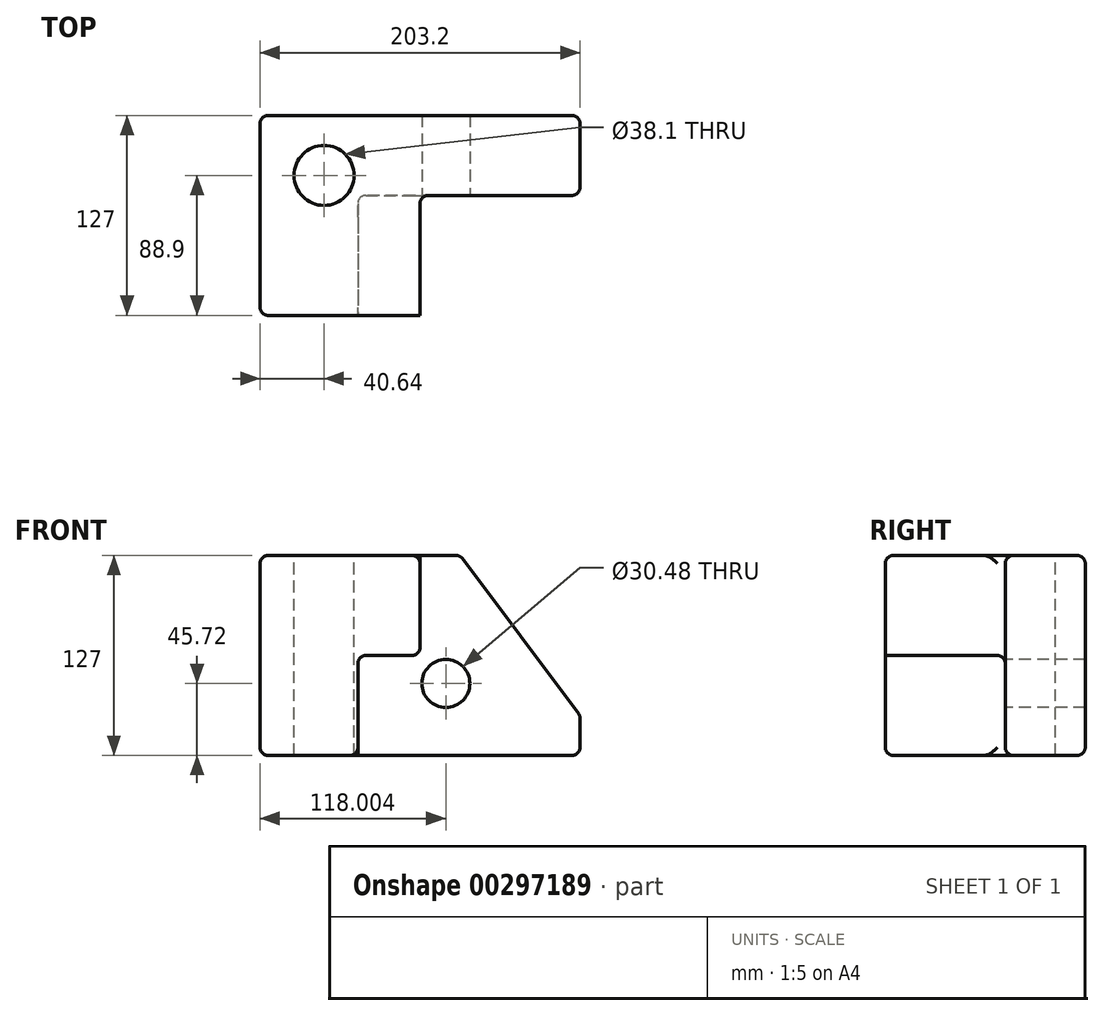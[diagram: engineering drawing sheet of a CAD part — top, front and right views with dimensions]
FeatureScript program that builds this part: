
annotation { "Feature Type Name" : "Feature", "Feature Type Description" : "" }
export const myFeature = defineFeature(function(context is Context, id is Id, definition is map)
    precondition{}
    {
        {
            var Q0;
            Q0=qCreatedBy(makeId("Front.planeOp"),FACE);
            var sketch = newSketch(context, id + "F0", { "sketchPlane" : qUnion([Q0])});
            skLineSegment(sketch, "E0.bottom", {"start": v(101.6, 63.5) * mm, "end": v(-101.6, 63.5) * mm});
            skLineSegment(sketch, "E0.top", {"start": v(101.6, -63.5) * mm, "end": v(-101.6, -63.5) * mm});
            skLineSegment(sketch, "E0.left", {"start": v(101.6, 63.5) * mm, "end": v(101.6, -63.5) * mm});
            skLineSegment(sketch, "E0.right", {"start": v(-101.6, 63.5) * mm, "end": v(-101.6, -63.5) * mm});
            skPoint(sketch, "E0.middle", {"position": v(0, 0) * mm});
            skSolve(sketch);
        }
        {
            var Q0;
            Q0 = qSketchRegion(id + "F0", true);
            extrude(context, id + "F1", {"entities" : qUnion([Q0]), "oppositeDirection" : true, "depth" : 127 * mm});
        }
        {
            var Q0;
            Q0=makeQuery(id+"F1.opExtrude","CAP_FACE",FACE,{"disambiguationData":[OSD([sQuery(id+"F0.wireOp",EDGE,"E0.bottom"),sQuery(id+"F0.wireOp",EDGE,"E0.top"),sQuery(id+"F0.wireOp",EDGE,"E0.left"),sQuery(id+"F0.wireOp",EDGE,"E0.right")])],"isStart":true});
            var sketch = newSketch(context, id + "F2", { "sketchPlane" : qUnion([Q0])});
            skLineSegment(sketch, "E1", {"start": v(-39.48, -63.5) * mm, "end": v(-39.48, 0) * mm});
            skLineSegment(sketch, "E2", {"start": v(-39.48, 0) * mm, "end": v(0, 0) * mm});
            skLineSegment(sketch, "E3", {"start": v(0, 0) * mm, "end": v(0, 63.5) * mm});
            skSolve(sketch);
        }
        {
            var Q0;
            {var subQ2=sQuery(id+"F2.wireOp",EDGE,"E1");Q0=makeQuery(id+"F2.imprint","IMPRINT",FACE,{"disambiguationData":[TD([[makeQuery(id+"F2.imprint","IMPRINT",EDGE,{"derivedFrom":subQ2}),-1.0]])]});}
            extrude(context, id + "F3", {"entities" : qUnion([Q0]), "operationType" : NewBodyOperationType.REMOVE, "oppositeDirection" : true, "depth" : 76.2 * mm});
        }
        {
            var Q0;
            Q0=makeQuery(id+"F1.opExtrude","SWEPT_EDGE",EDGE,{"disambiguationData":[OSD([sQuery(id+"F0.wireOp",EDGE,"E0.bottom"),sQuery(id+"F0.wireOp",EDGE,"E0.left")])]});
            chamfer(context, id + "F4", {"entities" : qUnion([Q0]), "chamferType" : ChamferType.TWO_OFFSETS, "width1" : 76.2 * mm, "oppositeDirection" : true, "width2" : 101.6 * mm, "tangentPropagation" : true});
        }
        {
            var Q0;
            Q0=makeQuery(id+"F1.opExtrude","SWEPT_EDGE",EDGE,{"disambiguationData":[OSD([sQuery(id+"F0.wireOp",EDGE,"E0.top"),sQuery(id+"F0.wireOp",EDGE,"E0.left")])]});
            var Q1;
            {var subQ0=sQuery(id+"F0.wireOp",EDGE,"E0.left");Q1=makeQuery(id+"F4.opChamfer","BLEND_EDGE",EDGE,{"blendedFrom":[makeQuery(id+"F1.opExtrude","SWEPT_EDGE",EDGE,{"disambiguationData":[OSD([sQuery(id+"F0.wireOp",EDGE,"E0.bottom"),subQ0])]}),makeQuery(id+"F1.opExtrude","SWEPT_FACE",FACE,{"disambiguationData":[OSD([subQ0])]})],"blendedInto":[makeQuery(id+"F1.opExtrude","SWEPT_FACE",FACE,{"disambiguationData":[OSD([subQ0])]})]});}
            var Q2;
            {var subQ0=sQuery(id+"F0.wireOp",EDGE,"E0.bottom");Q2=makeQuery(id+"F4.opChamfer","BLEND_EDGE",EDGE,{"blendedFrom":[makeQuery(id+"F1.opExtrude","SWEPT_EDGE",EDGE,{"disambiguationData":[OSD([subQ0,sQuery(id+"F0.wireOp",EDGE,"E0.left")])]}),makeQuery(id+"F1.opExtrude","SWEPT_FACE",FACE,{"disambiguationData":[OSD([subQ0])]})],"blendedInto":[makeQuery(id+"F1.opExtrude","SWEPT_FACE",FACE,{"disambiguationData":[OSD([subQ0])]})]});}
            var Q3;
            {var subQ0=sQuery(id+"F0.wireOp",EDGE,"E0.left");var subQ1=sQuery(id+"F0.wireOp",EDGE,"E0.bottom");Q3=makeQuery(id+"F4.opChamfer","BLEND_EDGE",EDGE,{"blendedFrom":[makeQuery(id+"F1.opExtrude","SWEPT_EDGE",EDGE,{"disambiguationData":[OSD([subQ1,subQ0])]}),makeQuery(id+"F3.boolean.opBoolean","COPY",FACE,{"derivedFrom":makeQuery(id+"F3.opExtrude","CAP_FACE",FACE,{"disambiguationData":[OSD([subQ1,sQuery(id+"F0.wireOp",EDGE,"E0.top"),subQ0,sQuery(id+"F2.wireOp",EDGE,"E1"),sQuery(id+"F2.wireOp",EDGE,"E2"),sQuery(id+"F2.wireOp",EDGE,"E3")])],"isStart":false})})],"blendedInto":[makeQuery(id+"F3.boolean.opBoolean","COPY",FACE,{"derivedFrom":makeQuery(id+"F3.opExtrude","CAP_FACE",FACE,{"disambiguationData":[OSD([subQ1,sQuery(id+"F0.wireOp",EDGE,"E0.top"),subQ0,sQuery(id+"F2.wireOp",EDGE,"E1"),sQuery(id+"F2.wireOp",EDGE,"E2"),sQuery(id+"F2.wireOp",EDGE,"E3")])],"isStart":false})})]});}
            var Q4;
            {var subQ0=sQuery(id+"F0.wireOp",EDGE,"E0.left");var subQ1=sQuery(id+"F0.wireOp",EDGE,"E0.bottom");Q4=makeQuery(id+"F4.opChamfer","BLEND_EDGE",EDGE,{"blendedFrom":[makeQuery(id+"F1.opExtrude","SWEPT_EDGE",EDGE,{"disambiguationData":[OSD([subQ1,subQ0])]}),makeQuery(id+"F1.opExtrude","CAP_FACE",FACE,{"disambiguationData":[OSD([subQ1,sQuery(id+"F0.wireOp",EDGE,"E0.top"),subQ0,sQuery(id+"F0.wireOp",EDGE,"E0.right")])],"isStart":false})],"blendedInto":[makeQuery(id+"F1.opExtrude","CAP_FACE",FACE,{"disambiguationData":[OSD([subQ1,sQuery(id+"F0.wireOp",EDGE,"E0.top"),subQ0,sQuery(id+"F0.wireOp",EDGE,"E0.right")])],"isStart":false})]});}
            var Q5;
            Q5=makeQuery(id+"F3.boolean.opBoolean","COPY",EDGE,{"derivedFrom":makeQuery(id+"F3.opExtrude","CAP_EDGE",EDGE,{"disambiguationData":[OSD([sQuery(id+"F0.wireOp",EDGE,"E0.bottom")])],"isStart":false})});
            var Q6;
            Q6=makeQuery(id+"F3.boolean.opBoolean","COPY",EDGE,{"derivedFrom":makeQuery(id+"F3.opExtrude","SWEPT_EDGE",EDGE,{"disambiguationData":[OSD([sQuery(id+"F0.wireOp",EDGE,"E0.bottom"),sQuery(id+"F2.wireOp",EDGE,"E3")])]})});
            var Q7;
            Q7=makeQuery(id+"F3.boolean.opBoolean","COPY",EDGE,{"derivedFrom":makeQuery(id+"F3.opExtrude","SWEPT_EDGE",EDGE,{"disambiguationData":[OSD([sQuery(id+"F2.wireOp",EDGE,"E2"),sQuery(id+"F2.wireOp",EDGE,"E3")])]})});
            var Q8;
            Q8=makeQuery(id+"F3.boolean.opBoolean","COPY",FACE,{"derivedFrom":makeQuery(id+"F3.opExtrude","CAP_FACE",FACE,{"disambiguationData":[OSD([sQuery(id+"F0.wireOp",EDGE,"E0.bottom"),sQuery(id+"F0.wireOp",EDGE,"E0.top"),sQuery(id+"F0.wireOp",EDGE,"E0.left"),sQuery(id+"F2.wireOp",EDGE,"E1"),sQuery(id+"F2.wireOp",EDGE,"E2"),sQuery(id+"F2.wireOp",EDGE,"E3")])],"isStart":false})});
            var Q9;
            Q9=makeQuery(id+"F3.boolean.opBoolean","COPY",EDGE,{"derivedFrom":makeQuery(id+"F3.opExtrude","CAP_EDGE",EDGE,{"disambiguationData":[OSD([sQuery(id+"F0.wireOp",EDGE,"E0.top")])],"isStart":false})});
            var Q10;
            Q10=makeQuery(id+"F3.boolean.opBoolean","COPY",EDGE,{"derivedFrom":makeQuery(id+"F3.opExtrude","CAP_EDGE",EDGE,{"disambiguationData":[OSD([sQuery(id+"F2.wireOp",EDGE,"E1")])],"isStart":true})});
            var Q11;
            Q11=makeQuery(id+"F3.boolean.opBoolean","COPY",EDGE,{"derivedFrom":makeQuery(id+"F3.opExtrude","CAP_EDGE",EDGE,{"disambiguationData":[OSD([sQuery(id+"F2.wireOp",EDGE,"E2")])],"isStart":true})});
            var Q12;
            Q12=makeQuery(id+"F1.opExtrude","CAP_EDGE",EDGE,{"disambiguationData":[OSD([sQuery(id+"F0.wireOp",EDGE,"E0.bottom")])],"isStart":true});
            var Q13;
            Q13=makeQuery(id+"F3.boolean.opBoolean","COPY",EDGE,{"derivedFrom":makeQuery(id+"F3.opExtrude","CAP_EDGE",EDGE,{"disambiguationData":[OSD([sQuery(id+"F2.wireOp",EDGE,"E3")])],"isStart":true})});
            var Q14;
            Q14=makeQuery(id+"F1.opExtrude","SWEPT_EDGE",EDGE,{"disambiguationData":[OSD([sQuery(id+"F0.wireOp",EDGE,"E0.bottom"),sQuery(id+"F0.wireOp",EDGE,"E0.right")])]});
            var Q15;
            Q15=makeQuery(id+"F1.opExtrude","CAP_EDGE",EDGE,{"disambiguationData":[OSD([sQuery(id+"F0.wireOp",EDGE,"E0.bottom")])],"isStart":false});
            var Q16;
            Q16=makeQuery(id+"F1.opExtrude","CAP_EDGE",EDGE,{"disambiguationData":[OSD([sQuery(id+"F0.wireOp",EDGE,"E0.top")])],"isStart":true});
            var Q17;
            Q17=makeQuery(id+"F1.opExtrude","CAP_EDGE",EDGE,{"disambiguationData":[OSD([sQuery(id+"F0.wireOp",EDGE,"E0.right")])],"isStart":true});
            var Q18;
            Q18=makeQuery(id+"F1.opExtrude","SWEPT_EDGE",EDGE,{"disambiguationData":[OSD([sQuery(id+"F0.wireOp",EDGE,"E0.top"),sQuery(id+"F0.wireOp",EDGE,"E0.right")])]});
            var Q19;
            Q19=makeQuery(id+"F3.boolean.opBoolean","COPY",EDGE,{"derivedFrom":makeQuery(id+"F3.opExtrude","SWEPT_EDGE",EDGE,{"disambiguationData":[OSD([sQuery(id+"F2.wireOp",EDGE,"E1"),sQuery(id+"F2.wireOp",EDGE,"E2")])]})});
            var Q20;
            Q20=makeQuery(id+"F3.boolean.opBoolean","COPY",EDGE,{"derivedFrom":makeQuery(id+"F3.opExtrude","CAP_EDGE",EDGE,{"disambiguationData":[OSD([sQuery(id+"F2.wireOp",EDGE,"E3")])],"isStart":false})});
            var Q21;
            Q21=makeQuery(id+"F3.boolean.opBoolean","COPY",EDGE,{"derivedFrom":makeQuery(id+"F3.opExtrude","CAP_EDGE",EDGE,{"disambiguationData":[OSD([sQuery(id+"F0.wireOp",EDGE,"E0.left")])],"isStart":false})});
            var Q22;
            Q22=makeQuery(id+"F1.opExtrude","CAP_EDGE",EDGE,{"disambiguationData":[OSD([sQuery(id+"F0.wireOp",EDGE,"E0.left")])],"isStart":false});
            var Q23;
            Q23=makeQuery(id+"F1.opExtrude","CAP_EDGE",EDGE,{"disambiguationData":[OSD([sQuery(id+"F0.wireOp",EDGE,"E0.top")])],"isStart":false});
            var Q24;
            Q24=makeQuery(id+"F3.boolean.opBoolean","COPY",EDGE,{"derivedFrom":makeQuery(id+"F3.opExtrude","SWEPT_EDGE",EDGE,{"disambiguationData":[OSD([sQuery(id+"F0.wireOp",EDGE,"E0.top"),sQuery(id+"F2.wireOp",EDGE,"E1")])]})});
            var Q25;
            Q25=makeQuery(id+"F3.boolean.opBoolean","COPY",EDGE,{"derivedFrom":makeQuery(id+"F3.opExtrude","CAP_EDGE",EDGE,{"disambiguationData":[OSD([sQuery(id+"F2.wireOp",EDGE,"E2")])],"isStart":false})});
            var Q26;
            Q26=makeQuery(id+"F1.opExtrude","CAP_EDGE",EDGE,{"disambiguationData":[OSD([sQuery(id+"F0.wireOp",EDGE,"E0.right")])],"isStart":false});
            var Q27;
            Q27=makeQuery(id+"F3.boolean.opBoolean","COPY",EDGE,{"derivedFrom":makeQuery(id+"F3.opExtrude","CAP_EDGE",EDGE,{"disambiguationData":[OSD([sQuery(id+"F2.wireOp",EDGE,"E1")])],"isStart":false})});
            fillet(context, id + "F5", {"entities" : qUnion([Q0, Q1, Q2, Q3, Q4, Q5, Q6, Q7, Q8, Q9, Q10, Q11, Q12, Q13, Q14, Q15, Q16, Q17, Q18, Q19, Q20, Q21, Q22, Q23, Q24, Q25, Q26, Q27]), "radius" : 5.08 * mm, "tangentPropagation" : true, "allowEdgeOverflow" : false});
        }
        {
            var Q0;
            Q0=makeQuery(id+"F3.boolean.opBoolean","COPY",FACE,{"derivedFrom":makeQuery(id+"F3.opExtrude","CAP_FACE",FACE,{"disambiguationData":[OSD([sQuery(id+"F0.wireOp",EDGE,"E0.bottom"),sQuery(id+"F0.wireOp",EDGE,"E0.top"),sQuery(id+"F0.wireOp",EDGE,"E0.left"),sQuery(id+"F2.wireOp",EDGE,"E1"),sQuery(id+"F2.wireOp",EDGE,"E2"),sQuery(id+"F2.wireOp",EDGE,"E3")])],"isStart":false})});
            var sketch = newSketch(context, id + "F6", { "sketchPlane" : qUnion([Q0])});
            skCircle(sketch, "E4", {"center": v(16.4, -17.78) * mm, "radius": 15.24 * mm});
            skSolve(sketch);
        }
        {
            var Q0;
            Q0=makeQuery(id+"F6.imprint","IMPRINT",FACE,{"disambiguationData":[TD([[makeQuery(id+"F6.imprint","IMPRINT",EDGE,{"derivedFrom":sQuery(id+"F6.wireOp",EDGE,"E4")}),1.0]])]});
            var Q1;
            Q1=sQuery(id+"F6.wireOp",EDGE,"E4");
            var Q2;
            Q2=makeQuery(id+"F1.opExtrude","CAP_FACE",FACE,{"disambiguationData":[OSD([sQuery(id+"F0.wireOp",EDGE,"E0.bottom"),sQuery(id+"F0.wireOp",EDGE,"E0.top"),sQuery(id+"F0.wireOp",EDGE,"E0.left"),sQuery(id+"F0.wireOp",EDGE,"E0.right")])],"isStart":false});
            extrude(context, id + "F7", {"entities" : qUnion([Q0]), "operationType" : NewBodyOperationType.REMOVE, "surfaceEntities" : qUnion([Q1]), "endBound" : BoundingType.UP_TO_SURFACE, "oppositeDirection" : true, "endBoundEntityFace" : qUnion([Q2]), "depth" : 25.4 * mm});
        }
        {
            var Q0;
            Q0=makeQuery(id+"F1.opExtrude","SWEPT_FACE",FACE,{"disambiguationData":[OSD([sQuery(id+"F0.wireOp",EDGE,"E0.bottom")])]});
            var sketch = newSketch(context, id + "F8", { "sketchPlane" : qUnion([Q0])});
            skCircle(sketch, "E5", {"center": v(-60.96, 88.9) * mm, "radius": 19.05 * mm});
            skSolve(sketch);
        }
        {
            var Q0;
            Q0=makeQuery(id+"F8.imprint","IMPRINT",FACE,{"disambiguationData":[TD([[makeQuery(id+"F8.imprint","IMPRINT",EDGE,{"derivedFrom":sQuery(id+"F8.wireOp",EDGE,"E5")}),1.0]])]});
            var Q1;
            Q1=sQuery(id+"F8.wireOp",EDGE,"E5");
            var Q2;
            Q2=makeQuery(id+"F1.opExtrude","SWEPT_FACE",FACE,{"disambiguationData":[OSD([sQuery(id+"F0.wireOp",EDGE,"E0.top")])]});
            extrude(context, id + "F9", {"entities" : qUnion([Q0]), "operationType" : NewBodyOperationType.REMOVE, "surfaceEntities" : qUnion([Q1]), "endBound" : BoundingType.UP_TO_SURFACE, "oppositeDirection" : true, "endBoundEntityFace" : qUnion([Q2]), "depth" : 25.4 * mm});
        }
    });
